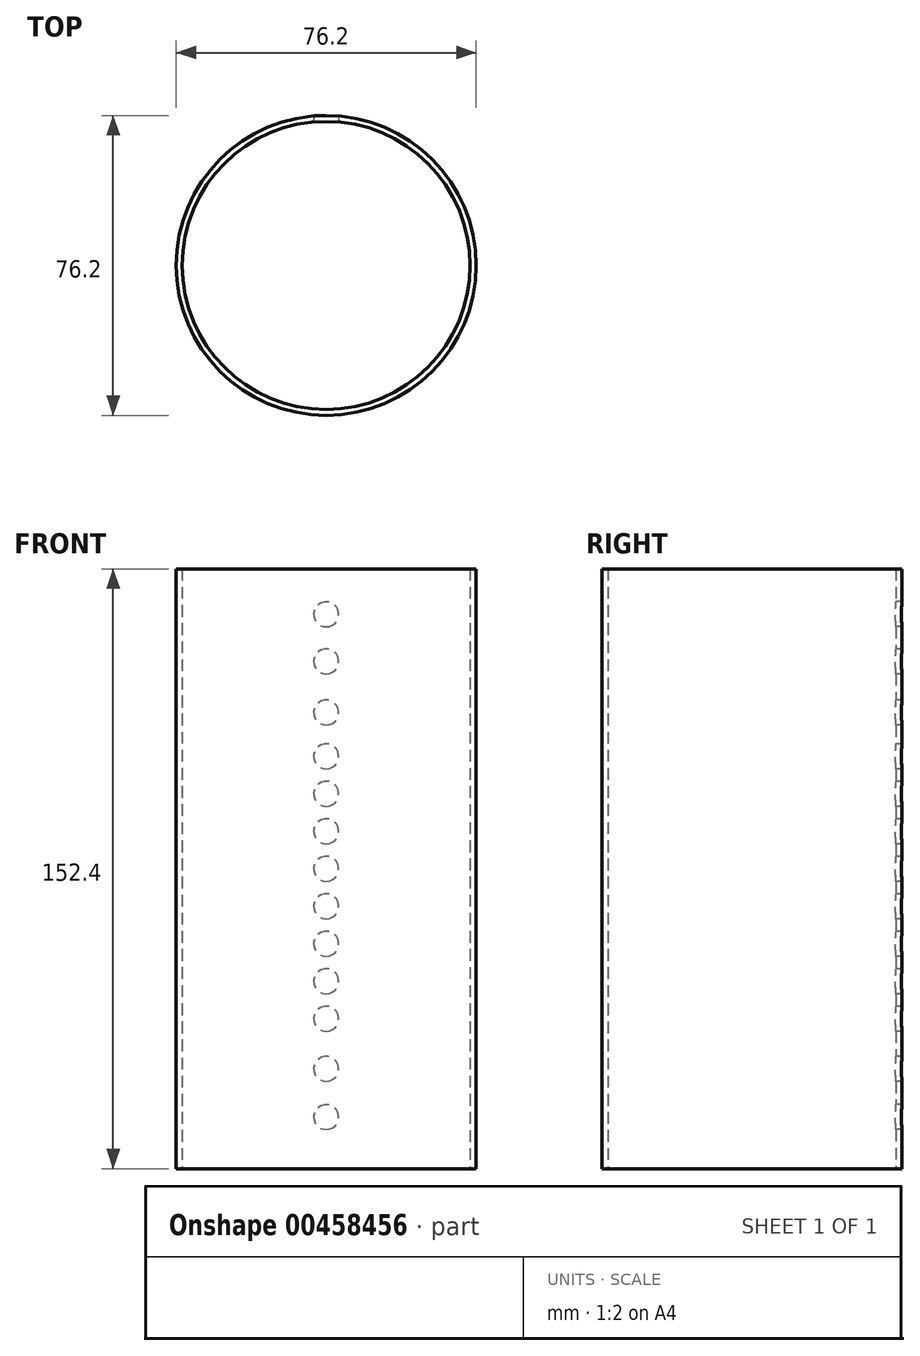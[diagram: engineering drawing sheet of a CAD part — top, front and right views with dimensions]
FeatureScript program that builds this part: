
annotation { "Feature Type Name" : "Feature", "Feature Type Description" : "" }
export const myFeature = defineFeature(function(context is Context, id is Id, definition is map)
    precondition{}
    {
        {
            var Q0;
            Q0=qCreatedBy(makeId("Top.planeOp"),FACE);
            var sketch = newSketch(context, id + "F0", { "sketchPlane" : qUnion([Q0])});
            skCircle(sketch, "E0", {"center": v(0, 0) * mm, "radius": 38.1 * mm});
            skCircle(sketch, "E1", {"center": v(0, 0) * mm, "radius": 36.58 * mm});
            skSolve(sketch);
        }
        {
            var Q0;
            Q0 = qSketchRegion(id + "F0", true);
            extrude(context, id + "F1", {"entities" : qUnion([Q0]), "endBound" : BoundingType.SYMMETRIC, "depth" : 152.4 * mm});
        }
        {
            var Q0;
            Q0=qCreatedBy(makeId("Front.planeOp"),FACE);
            var sketch = newSketch(context, id + "F2", { "sketchPlane" : qUnion([Q0])});
            skCircle(sketch, "E2", {"center": v(0, 0) * mm, "radius": 3.18 * mm});
            skCircle(sketch, "E3.0.1.0", {"center": v(0, -9.53) * mm, "radius": 3.18 * mm});
            skLineSegment(sketch, "E3.direction2", {"start": v(0, 0) * mm, "end": v(0, -9.53) * mm, "construction": true});
            skCircle(sketch, "E4.0.0.2", {"center": v(0, -19.05) * mm, "radius": 3.18 * mm});
            skCircle(sketch, "E5", {"center": v(0, 9.53) * mm, "radius": 3.18 * mm});
            skCircle(sketch, "E6", {"center": v(0, 19.05) * mm, "radius": 3.18 * mm});
            skCircle(sketch, "E7", {"center": v(0, 28.58) * mm, "radius": 3.18 * mm});
            skCircle(sketch, "E8", {"center": v(0, -28.58) * mm, "radius": 3.18 * mm});
            skCircle(sketch, "E9", {"center": v(0, 39.68) * mm, "radius": 3.18 * mm});
            skCircle(sketch, "E10", {"center": v(0, 52.69) * mm, "radius": 3.18 * mm});
            skCircle(sketch, "E11", {"center": v(0, 64.66) * mm, "radius": 3.18 * mm});
            skCircle(sketch, "E12", {"center": v(0, -38.1) * mm, "radius": 3.18 * mm});
            skCircle(sketch, "E13", {"center": v(0, -50.87) * mm, "radius": 3.18 * mm});
            skCircle(sketch, "E14", {"center": v(0, -63.1) * mm, "radius": 3.18 * mm});
            skSolve(sketch);
        }
        {
            var Q0;
            Q0 = qSketchRegion(id + "F2", true);
            extrude(context, id + "F3", {"entities" : qUnion([Q0]), "operationType" : NewBodyOperationType.REMOVE, "endBound" : BoundingType.THROUGH_ALL, "oppositeDirection" : true, "depth" : 25.4 * mm});
        }
        {
            var Q0;
            Q0=qCreatedBy(makeId("Right.planeOp"),FACE);
            var sketch = newSketch(context, id + "F4", { "sketchPlane" : qUnion([Q0])});
            skLineSegment(sketch, "E15", {"start": v(0, 59.97) * mm, "end": v(0, -54) * mm, "construction": true});
            skSolve(sketch);
        }
    });
